# Revit family: Armor AWH0400-1000
name_source: partatom
category: Mechanical Equipment
revit_build: Autodesk Revit 2017 (Build: 20190507_1515(x64)
units: mm (PartAtom-declared; Revit-internal decimal feet)

## family parameters
Always vertical = Yes
Cut with Voids When Loaded = No
OmniClass Number = 23.65.35.11.17
OmniClass Title = Thermodynamic Water Heaters
Part Type = Normal
Room Calculation Point = No
Round Connector Dimension = Use Radius
Shared = No
Work Plane-Based = No

## types (5) — shared parameters
A_HEIGHT = 45"
B_WIDTH = 24"
Back Clearance Depth = 24"
Clearance Display = Yes
Condensate Drain Offset From Bottom = 5 3/4"
Condensate Drain Offset From Right = 10 1/2"
Condensate Drain Radius = 3/8"
Description = Armor Condensing Commercial Gas Water Heater
FUEL TYPE = NATURAL GAS
Front Clearance Depth = 24"
Fuel Type = Natural or LP
G_Air Inlet Offset From Bottom = 12"
H_Air Inlet Offset From Right = 20"
I_Water Conn Offset from Bottom = 38"
J_Water Outlet Offset From Right = 3 1/2"
K_Flue Offset From Right = 10 1/2"
L_Flue Offset From Bottom = 19 1/4"
Left Clearance Depth = 0"
M_Water Inlet Offset from Right = 20"
Manufacturer = Lochinvar
Outside Gas Conn Offset from Bottom = 6"
Outside Gas Conn Offset from Front = 5"
Right Clearance Depth = 0"
SES BIM Studio # = 20 0649 01
Top Clearance Depth = 24"
URL = https://www.lochinvar.com
Voltage & Phase / Heater = 120V / 1ø
Voltage & Phase / Pump = 120V / 1ø
Voltage/Control = 24

## per-type parameters (varying)
| type | AIR INLET SIZE | Air Inlet Radius | C_DEPTH | D_Unit Depth plus Water Outlet Length | E_Gas Conn Offset from Bottom | FLOW RATE (GPM) | FRICTION LOSS (FT HD) | F_Gas Conn Offset From Right | Flue Radius | GALLON CAPACITY | GAS CONN SIZE | Gas Conn Radius | INPUT RATE (BTUH) | VENT SIZE | WATER CONN SIZE | WEIGHT | Water Conn Radius |
| AWH0400NPM | 4" | 2" | 30 1/2" | 42 1/2" | 29 3/4" | 35 | 9 | 20 1/4" | 2" | 4.4 | 1" | 1/2" | 399,000 | 4" | 2" | 326 | 1" |
| AWH0500NPM | 4" | 2" | 30 1/2" | 42 1/2" | 29 3/4" | 37 | 16 | 20 1/4" | 2" | 4.9 | 1" | 1/2" | 500,000 | 4" | 2" | 333 | 1" |
| AWH0650NPM | 4" | 2" | 41" | 53" | 30 1/2" | 44 | 15 | 15 1/4" | 2" | 6.2 | 1 1/4" | 5/8" | 650,000 | 4" | 2" | 424 | 1" |
| AWH0800NPM | 4" | 2" | 41" | 53" | 30 1/2" | 61 | 22 | 15 1/4" | 3" | 7.3 | 1 1/4" | 5/8" | 800,000 | 6" | 2" | 433 | 1" |
| AWH1000NPM | 6" | 3" | 48" | 62" | 30 1/2" | 79 | 15 | 15 3/4" | 3" | 8.8 | 1 1/4" | 5/8" | 999,000 | 6" | 2 1/2" | 494 | 1 1/4" |

note: column(s) folded — value = type name in every type: MODEL NO., Model

## geometry (parser evidence)
native form markers: Sweep x2
no freeform markers — native parametric forms only
